# Revit family: Enave 210 270 V
name_source: partatom
category: Mechanical Equipment
units: mm (PartAtom-declared; Revit-internal decimal feet)

## family parameters
Always vertical = Yes
Cut with Voids When Loaded = No
OmniClass Number = 23.75.00.00
OmniClass Title = Climate Control (HVAC)
Part Type = Normal
Room Calculation Point = No
Round Connector Dimension = Use Diameter
Shared = No
Work Plane-Based = No

## types (8) — shared parameters
00_20_Manufacturer = Vents
00_20_Name = Air handling unit
Air Flow (default) = 0.0 m³/h
Casing Material = Polypropylene (black)
D = 122 mm  [stored 0.400262 ft]
Filter = G4 / Coarse > 60%
Frequency = 60 Hz
H = 900 mm  [stored 2.95276 ft]
H1 = 958 mm  [stored 3.14304 ft]
L = 452 mm  [stored 1.48294 ft]
L1 = 190 mm
Load Classification = HVAC
Maintenance zone material = <By Category>
Number of Fase = 1
Pressure_Static_Air = 0.0 Pa
Voltage = 230 V
W = 598 mm  [stored 1.96194 ft]
W1 = 273 mm  [stored 0.895669 ft]
zero-valued in all types: Default Elevation

## per-type parameters (varying)
| type | Amperage | Maximum Air Flow | Power | Sound pressure level at 3 m distance | Weight |
| Enave 210 V | 1 A | 277.0 m³/h | 125 W | 31 dBA | 20.00 kg |
| Enave-T 210 V | 1 A | 277.0 m³/h | 125 W | 31 dBA | 22.00 kg |
| Enave 210 VE | 5 A | 277.0 m³/h | 925 W | 31 dBA | 20.00 kg |
| Enave-T 210 VE | 5 A | 277.0 m³/h | 925 W | 31 dBA | 22.00 kg |
| Enave 270 V | 1 A | 331.0 m³/h | 182 W | 34 dBA | 22.00 kg |
| Enave-T 270 V | 1 A | 331.0 m³/h | 182 W | 34 dBA | 24.00 kg |
| Enave 270 VE | 8 A | 331.0 m³/h | 1582 W | 34 dBA | 22.00 kg |
| Enave-T 270 VE | 8 A | 331.0 m³/h | 1582 W | 34 dBA | 24.00 kg |

note: column(s) folded — value = type name in every type: 00_20_Type

note: [stored X ft] marks values corroborated as IEEE doubles in the binary element streams (Revit-internal decimal feet)

## geometry (parser evidence)
native form markers: Sweep x14
no freeform markers — native parametric forms only
